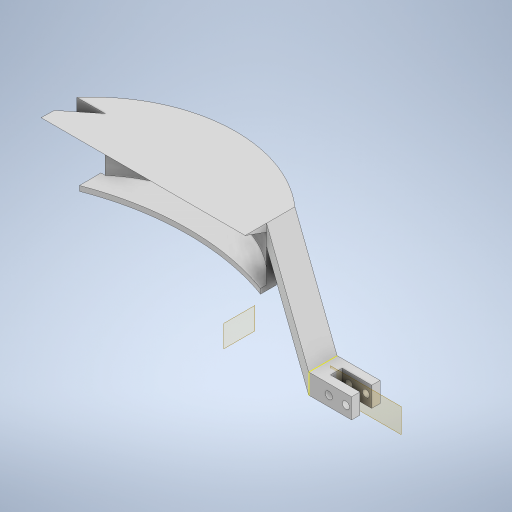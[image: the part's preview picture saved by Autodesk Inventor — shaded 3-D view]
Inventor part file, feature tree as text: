
AUTODESK INVENTOR PART (.ipt)
format: ipt  version: 2024.3 (Build 283343000, 343)  size: 316,416 bytes
history: native  units: mm
features: sketch x6, other x3, plane x2, extrude x1
ambient origin geometry x8: Origin, YZ Plane, XZ Plane, XY Plane, X Axis, Y Axis, Z Axis, Center Point
bodies: Solid1 (feature_tree)
feature tree (12):
  other  "pinzatula1.ipt"
  extrude  "Extrusion1"  Depth=10.0mm
  other  "Solid1::pinzatula1.ipt"
  other  "TaggingFeature1"
  sketch  "Sketch1"  dims[d0=10.0mm d1=0.3mm]
  sketch  "Sketch2"  dims[d2=0.3mm]
  sketch  "Sketch3"  dims[d3=100.0mm d4=0.0mm]
  sketch  "Sketch4"
  sketch  "Sketch5"
  plane  "Work Plane1"
  plane  "Work Plane2"
  sketch  "Sketch6"
